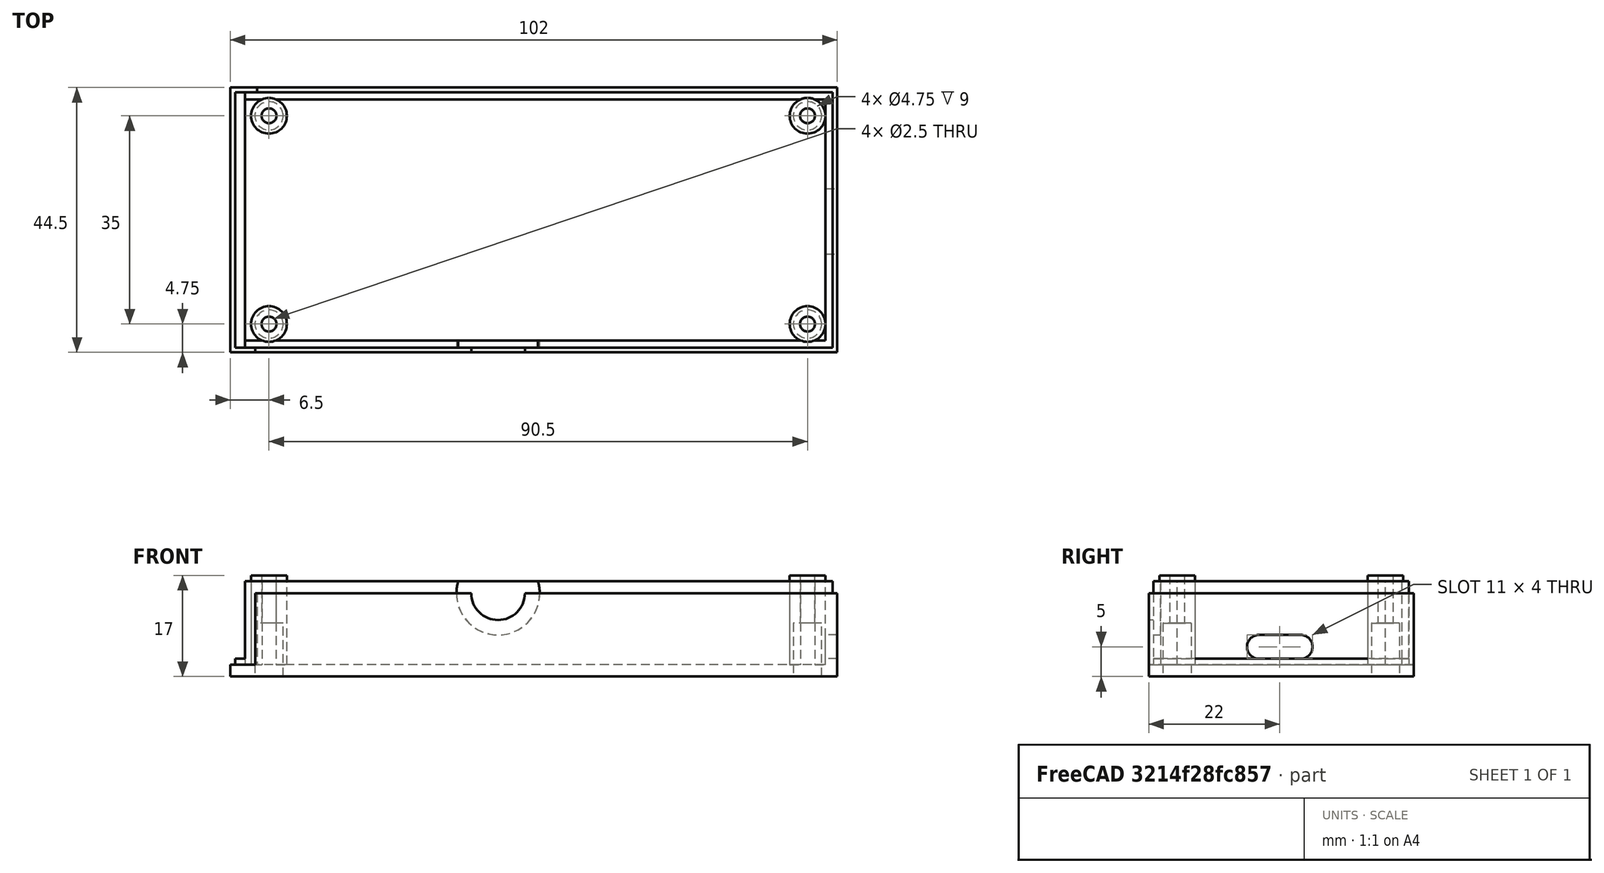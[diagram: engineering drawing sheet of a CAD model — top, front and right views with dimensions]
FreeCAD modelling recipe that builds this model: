
FCSTD DOCUMENT  (FreeCAD 0.20R)
Label: upper_no_battery
License: All rights reserved
LicenseURL: http://en.wikipedia.org/wiki/All_rights_reserved
objects: Sketcher::SketchObject×11, PartDesign::Pocket×9, PartDesign::Pad×2, PartDesign::Plane×1, PartDesign::Body×1
note: 35 computed .brp shape members not serialized (recipe doc carries the construction recipe); baked Part::Feature solids carry a one-line shape summary decoded from their .brp

FEATURE [Sketcher::SketchObject] Sketch  label="sketch_lower_base"
  FullyConstrained = true
  MapMode = 5
  Support = -> [XY_Plane]
  sketch-geometry (4):
    g0: LineSegment StartX=0 StartY=0 StartZ=0 EndX=102 EndY=0 EndZ=0
    g1: LineSegment StartX=102 StartY=0 StartZ=0 EndX=102 EndY=44.5 EndZ=0
    g2: LineSegment StartX=102 StartY=44.5 StartZ=0 EndX=0 EndY=44.5 EndZ=0
    g3: LineSegment StartX=0 StartY=44.5 StartZ=0 EndX=0 EndY=0 EndZ=0
  constraints (11):
    c: Coincident(g0,g1)
    c: Coincident(g1,g2)
    c: Coincident(g2,g3)
    c: Coincident(g3,g0)
    c: Horizontal(g0)
    c: Horizontal(g2)
    c: Vertical(g1)
    c: Vertical(g3)
    c: Coincident(g0,g-1)
    c: Distance(g2) = 102
    c: Distance(g3) = 44.5
FEATURE [PartDesign::Pad] Pad  label="pad_lower_base"
  Direction = (0,0,1)
  Length = 16
  Length2 = 10
  Profile = -> Sketch
  ReferenceAxis = -> Sketch [N_Axis]
  Type = 0
FEATURE [Sketcher::SketchObject] Sketch001  label="sketch_lower_base_hole"
  FullyConstrained = true
  MapMode = 5
  Placement = pos=(0,0,16) rot=(0,0,1;0rad)
  Support = -> [Pad]
  sketch-geometry (4):
    g0: LineSegment StartX=2.5 StartY=42.5 StartZ=0 EndX=100 EndY=42.5 EndZ=0
    g1: LineSegment StartX=100 StartY=42.5 StartZ=0 EndX=100 EndY=2 EndZ=0
    g2: LineSegment StartX=100 StartY=2 StartZ=0 EndX=2.5 EndY=2 EndZ=0
    g3: LineSegment StartX=2.5 StartY=2 StartZ=0 EndX=2.5 EndY=42.5 EndZ=0
  constraints (12):
    c: Coincident(g0,g1)
    c: Coincident(g1,g2)
    c: Coincident(g2,g3)
    c: Coincident(g3,g0)
    c: Horizontal(g0)
    c: Horizontal(g2)
    c: Vertical(g1)
    c: Vertical(g3)
    c: DistanceX(g-2,g2) = 2.5
    c: DistanceY(g-1,g2) = 2
    c: Distance(g0) = 97.5
    c: Distance(g1) = 40.5
FEATURE [PartDesign::Pocket] Pocket  label="pocket_lower_base_hole"
  BaseFeature = -> Pad
  Direction = (0,0,-1)
  Length = 14
  Length2 = 5
  Profile = -> Sketch001
  ReferenceAxis = -> Sketch001 [N_Axis]
  Type = 0
FEATURE [Sketcher::SketchObject] Sketch002  label="sketch_board_stands"
  FullyConstrained = true
  MapMode = 5
  Placement = pos=(0,0,2) rot=(0,0,1;0rad)
  Support = -> [Pocket]
  sketch-geometry (4):
    g0: Circle CenterX=6.5 CenterY=39.75 CenterZ=0 NormalX=0 NormalY=0 NormalZ=1 AngleXU=0 Radius=3
    g1: Circle CenterX=97 CenterY=39.75 CenterZ=0 NormalX=0 NormalY=0 NormalZ=1 AngleXU=0 Radius=3
    g2: Circle CenterX=6.5 CenterY=4.75 CenterZ=0 NormalX=0 NormalY=0 NormalZ=1 AngleXU=0 Radius=3
    g3: Circle CenterX=97 CenterY=4.75 CenterZ=0 NormalX=0 NormalY=0 NormalZ=1 AngleXU=0 Radius=3
  constraints (12):
    c: Equal(g0,g1)
    c: Equal(g1,g3)
    c: Equal(g3,g2)
    c: Distance(g0,g1) = 90.5
    c: Distance(g2,g3) = 90.5
    c: Diameter(g1) = 6
    c: Distance(g1,g3) = 35
    c: Distance(g0,g2) = 35
    c: DistanceX(g-2,g1) = 97
    c: DistanceX(g-2,g3) = 97
    c: DistanceY(g-1,g2) = 4.75
    c: DistanceY(g-1,g3) = 4.75
FEATURE [PartDesign::Pad] Pad001  label="pad_board_stands"
  BaseFeature = -> Pocket
  Direction = (0,0,1)
  Length = 15
  Length2 = 10
  Profile = -> Sketch002
  ReferenceAxis = -> Sketch002 [N_Axis]
  Type = 0
FEATURE [PartDesign::Plane] DatumPlane  label="plane_upper"
  Length = 145.79
  MapMode = 5
  Placement = pos=(0,0,-18) rot=(1,0,0;3.14159rad)
  ResizeMode = 0
  Width = 88.2899
FEATURE [Sketcher::SketchObject] Sketch007  label="sketch_screw_holes"
  FullyConstrained = true
  MapMode = 5
  Placement = pos=(0,0,-18) rot=(1,0,0;3.14159rad)
  Support = -> [DatumPlane]
  sketch-geometry (4):
    g0: Circle CenterX=6.5 CenterY=-4.75 CenterZ=0 NormalX=0 NormalY=0 NormalZ=1 AngleXU=0 Radius=1.25
    g1: Circle CenterX=97 CenterY=-4.75 CenterZ=0 NormalX=0 NormalY=0 NormalZ=1 AngleXU=0 Radius=1.25
    g2: Circle CenterX=6.5 CenterY=-39.75 CenterZ=0 NormalX=0 NormalY=0 NormalZ=1 AngleXU=0 Radius=1.25
    g3: Circle CenterX=97 CenterY=-39.75 CenterZ=0 NormalX=0 NormalY=0 NormalZ=1 AngleXU=0 Radius=1.25
  constraints (12):
    c: Equal(g0,g2)
    c: Equal(g2,g3)
    c: Equal(g3,g1)
    c: Diameter(g0) = 2.5
    c: Distance(g3,g1) = 35
    c: Distance(g0,g2) = 35
    c: Distance(g0,g1) = 90.5
    c: Distance(g2,g3) = 90.5
    c: DistanceY(g-1,g0) = -4.75
    c: DistanceY(g-1,g1) = -4.75
    c: DistanceX(g-2,g1) = 97
    c: DistanceX(g-2,g3) = 97
FEATURE [PartDesign::Pocket] Pocket004  label="pocket_screw_holes"
  BaseFeature = -> Pad001
  Direction = (0,0,1)
  Length = 35
  Length2 = 5
  Profile = -> Sketch007
  ReferenceAxis = -> Sketch007 [N_Axis]
  Type = 0
FEATURE [Sketcher::SketchObject] Sketch008  label="sketch_screwdriver_hole"
  FullyConstrained = true
  MapMode = 5
  Placement = pos=(0,0,-18) rot=(1,0,0;3.14159rad)
  Support = -> [DatumPlane]
  sketch-geometry (4):
    g0: Circle CenterX=6.5 CenterY=-4.75 CenterZ=0 NormalX=0 NormalY=0 NormalZ=1 AngleXU=0 Radius=2.375
    g1: Circle CenterX=97 CenterY=-4.75 CenterZ=0 NormalX=0 NormalY=0 NormalZ=1 AngleXU=0 Radius=2.375
    g2: Circle CenterX=6.5 CenterY=-39.75 CenterZ=0 NormalX=0 NormalY=0 NormalZ=1 AngleXU=0 Radius=2.375
    g3: Circle CenterX=97 CenterY=-39.75 CenterZ=0 NormalX=0 NormalY=0 NormalZ=1 AngleXU=0 Radius=2.375
  constraints (12):
    c: Diameter(g0) = 4.75
    c: Equal(g0,g1)
    c: Equal(g1,g2)
    c: Equal(g2,g3)
    c: DistanceY(g-1,g0) = -4.75
    c: DistanceY(g-1,g1) = -4.75
    c: Distance(g3,g2) = 90.5
    c: Distance(g0,g1) = 90.5
    c: Distance(g1,g3) = 35
    c: Distance(g2,g0) = 35
    c: DistanceX(g-2,g3) = 97
    c: DistanceX(g-2,g1) = 97
FEATURE [PartDesign::Pocket] Pocket005  label="pocket_screwdriver_hole"
  BaseFeature = -> Pocket004
  Direction = (0,0,1)
  Length = 27
  Length2 = 5
  Profile = -> Sketch008
  ReferenceAxis = -> Sketch008 [N_Axis]
  Type = 0
FEATURE [Sketcher::SketchObject] Sketch011  label="sketch_esp_usb_hole"
  FullyConstrained = true
  MapMode = 5
  Placement = pos=(102,0,0) rot=(0.57735,0.57735,0.57735;2.0944rad)
  sketch-geometry (4):
    g0: ArcOfCircle CenterX=18.5 CenterY=5 CenterZ=0 NormalX=0 NormalY=0 NormalZ=1 AngleXU=0 Radius=2 StartAngle=1.5708 EndAngle=4.71239
    g1: ArcOfCircle CenterX=25.5 CenterY=5 CenterZ=0 NormalX=0 NormalY=0 NormalZ=1 AngleXU=0 Radius=2 StartAngle=4.71239 EndAngle=7.85398
    g2: LineSegment StartX=18.5 StartY=3 StartZ=0 EndX=25.5 EndY=3 EndZ=0
    g3: LineSegment StartX=25.5 StartY=7 StartZ=0 EndX=18.5 EndY=7 EndZ=0
  constraints (10):
    c: Tangent(g0,g2) = -1.5708
    c: Tangent(g2,g1) = -1.5708
    c: Tangent(g1,g3) = -1.5708
    c: Tangent(g3,g0) = -1.5708
    c: Equal(g0,g1)
    c: Horizontal(g2)
    c: Radius(g1) = 2
    c: Distance(g0,g1) = 7
    c: DistanceY(g-1,g0) = 3
    c: DistanceX(g-2,g0) = 18.5
FEATURE [PartDesign::Pocket] Pocket008  label="pocket_esp_usb_hole"
  BaseFeature = -> Pocket005
  Direction = (-1,0,0)
  Length = 5
  Length2 = 5
  Profile = -> Sketch011
  ReferenceAxis = -> Sketch011 [N_Axis]
  Type = 0
FEATURE [Sketcher::SketchObject] Sketch012  label="sketch_ptt_hole"
  FullyConstrained = true
  MapMode = 5
  Placement = pos=(0,0,0) rot=(1,0,0;1.5708rad)
  Support = -> [Pocket008]
  sketch-geometry (1):
    g0: Circle CenterX=45 CenterY=14 CenterZ=0 NormalX=0 NormalY=0 NormalZ=1 AngleXU=0 Radius=4.5
  constraints (3):
    c: DistanceY(g-1,g0) = 14
    c: Diameter(g0) = 9
    c: DistanceX(g-2,g0) = 45
FEATURE [PartDesign::Pocket] Pocket009  label="pocket_ptt_hole"
  BaseFeature = -> Pocket008
  Direction = (0,1,-2e-16)
  Length = 10
  Length2 = 5
  Profile = -> Sketch012
  ReferenceAxis = -> Sketch012 [N_Axis]
  Type = 0
FEATURE [Sketcher::SketchObject] Sketch013  label="sketch_ptt_hole_rounding"
  FullyConstrained = true
  MapMode = 5
  Placement = pos=(0,2,0) rot=(0,0.707107,0.707107;3.14159rad)
  Support = -> [Pocket009]
  sketch-geometry (1):
    g0: Circle CenterX=-45 CenterY=14 CenterZ=0 NormalX=0 NormalY=0 NormalZ=1 AngleXU=0 Radius=7
  constraints (3):
    c: DistanceX(g-2,g0) = -45
    c: DistanceY(g-1,g0) = 14
    c: Diameter(g0) = 14
FEATURE [PartDesign::Pocket] Pocket010  label="pocket_ptt_hole_rounding"
  BaseFeature = -> Pocket009
  Direction = (0,-1,2e-16)
  Length = 1.2
  Length2 = 5
  Profile = -> Sketch013
  ReferenceAxis = -> Sketch013 [N_Axis]
  Type = 0
FEATURE [Sketcher::SketchObject] Sketch022  label="sketch_face_removal"
  FullyConstrained = true
  MapMode = 5
  Placement = pos=(0,0,16) rot=(0,0,1;0rad)
  sketch-geometry (4):
    g0: LineSegment StartX=0 StartY=44.5 StartZ=0 EndX=2.5 EndY=44.5 EndZ=0
    g1: LineSegment StartX=2.5 StartY=44.5 StartZ=0 EndX=2.5 EndY=0 EndZ=0
    g2: LineSegment StartX=2.5 StartY=0 StartZ=0 EndX=0 EndY=0 EndZ=0
    g3: LineSegment StartX=0 StartY=0 StartZ=0 EndX=0 EndY=44.5 EndZ=0
  constraints (12):
    c: Coincident(g0,g1)
    c: Coincident(g1,g2)
    c: Coincident(g2,g3)
    c: Coincident(g3,g0)
    c: Horizontal(g0)
    c: Horizontal(g2)
    c: Vertical(g1)
    c: Vertical(g3)
    c: PointOnObject(g0,g-2)
    c: PointOnObject(g1,g-1)
    c: Distance(g0) = 2.5
    c: Distance(g1) = 44.5
FEATURE [PartDesign::Pocket] Pocket018  label="pocket_face_removal"
  BaseFeature = -> Pocket010
  Direction = (0,0,-1)
  Length = 13
  Length2 = 5
  Profile = -> Sketch022
  ReferenceAxis = -> Sketch022 [N_Axis]
  Type = 0
FEATURE [Sketcher::SketchObject] Sketch023  label="sketch_outer_facet_removal"
  FullyConstrained = false
  MapMode = 5
  Placement = pos=(0,0,16) rot=(0,0,1;0rad)
  Support = -> [Pocket018]
  sketch-geometry (8):
    g0: LineSegment StartX=2.49905 StartY=44.5 StartZ=0 EndX=102 EndY=44.5 EndZ=0
    g1: LineSegment StartX=102 StartY=44.5 StartZ=0 EndX=102 EndY=0 EndZ=0
    g2: LineSegment StartX=102 StartY=0 StartZ=0 EndX=2.5 EndY=0 EndZ=0
    g3: LineSegment StartX=2.5 StartY=0 StartZ=0 EndX=2.5 EndY=0.8 EndZ=0
    g4: LineSegment StartX=2.5 StartY=0.8 StartZ=0 EndX=101.2 EndY=0.8 EndZ=0
    g5: LineSegment StartX=101.2 StartY=0.8 StartZ=0 EndX=101.2 EndY=43.7 EndZ=0
    g6: LineSegment StartX=101.2 StartY=43.7 StartZ=0 EndX=2.49905 EndY=43.7 EndZ=0
    g7: LineSegment StartX=2.49905 StartY=43.7 StartZ=0 EndX=2.49905 EndY=44.5 EndZ=0
  constraints (23):
    c: Horizontal(g0)
    c: Coincident(g1,g0)
    c: Vertical(g1)
    c: Coincident(g2,g1)
    c: PointOnObject(g2,g-1)
    c: Horizontal(g2)
    c: Coincident(g3,g2)
    c: Vertical(g3)
    c: Coincident(g4,g3)
    c: Horizontal(g4)
    c: Coincident(g5,g4)
    c: Vertical(g5)
    c: Coincident(g6,g5)
    c: Horizontal(g6)
    c: Coincident(g7,g6)
    c: Coincident(g7,g0)
    c: Vertical(g7)
    c: Distance(g7) = 0.8
    c: Equal(g7,g3)
    c: Distance(g5,g1) = 0.8
    c: DistanceX(g-2,g2) = 2.5
    c: DistanceY(g-1,g0) = 44.5
    c: DistanceX(g-2,g0) = 102
FEATURE [PartDesign::Pocket] Pocket019  label="pocket_outer_facet_removal"
  BaseFeature = -> Pocket018
  Direction = (0,0,-1)
  Length = 2
  Length2 = 5
  Profile = -> Sketch023
  ReferenceAxis = -> Sketch023 [N_Axis]
  Type = 0
FEATURE [Sketcher::SketchObject] Sketch024  label="sketch_outer_front_facet_removal"
  FullyConstrained = false
  MapMode = 5
  Placement = pos=(0,0,16) rot=(0,0,1;0rad)
  Support = -> [Pocket019]
  sketch-geometry (8):
    g0: LineSegment StartX=4.16371 StartY=0 StartZ=0 EndX=4.16371 EndY=0.8 EndZ=0
    g1: LineSegment StartX=4.16371 StartY=0.8 StartZ=0 EndX=0.800622 EndY=0.8 EndZ=0
    g2: LineSegment StartX=0.800622 StartY=0.8 StartZ=0 EndX=0.800622 EndY=43.7 EndZ=0
    g3: LineSegment StartX=0.800622 StartY=43.7 StartZ=0 EndX=4.5 EndY=43.7 EndZ=0
    g4: LineSegment StartX=4.5 StartY=43.7 StartZ=0 EndX=4.5 EndY=44.5 EndZ=0
    g5: LineSegment StartX=4.5 StartY=44.5 StartZ=0 EndX=0 EndY=44.5 EndZ=0
    g6: LineSegment StartX=0 StartY=44.5 StartZ=0 EndX=0 EndY=0 EndZ=0
    g7: LineSegment StartX=0 StartY=0 StartZ=0 EndX=4.16371 EndY=0 EndZ=0
  constraints (21):
    c: Coincident(g4,g5)
    c: Coincident(g4,g3)
    c: Coincident(g6,g5)
    c: Coincident(g2,g3)
    c: Coincident(g1,g2)
    c: Coincident(g1,g0)
    c: Coincident(g0,g7)
    c: Coincident(g7,g6)
    c: Distance(g4) = 0.8
    c: Distance(g0) = 0.8
    c: Parallel(g6,g2)
    c: Parallel(g2,g0)
    c: Parallel(g0,g4)
    c: Parallel(g4,g-2)
    c: Parallel(g5,g3)
    c: Parallel(g3,g1)
    c: Parallel(g1,g7)
    c: Parallel(g7,g-1)
    c: Distance(g5) = 4.5
    c: Coincident(g6,g-1)
    c: Distance(g6) = 44.5
FEATURE [PartDesign::Pocket] Pocket020  label="pocket_outer_front_facet_removal"
  BaseFeature = -> Pocket019
  Direction = (0,0,-1)
  Length = 14
  Length2 = 5
  Profile = -> Sketch024
  ReferenceAxis = -> Sketch024 [N_Axis]
  Type = 0
FEATURE [PartDesign::Body] Body
  Group = -> [Sketch,Pad,Sketch001,Pocket,Sketch002,Pad001,DatumPlane,Sketch007,Pocket004,Sketch008,Pocket005,Sketch011,Pocket008,Sketch012,Pocket009,Sketch013,Pocket010,Sketch022,Pocket018,Sketch023,Pocket019,Sketch024,Pocket020]
  Origin = -> Origin
  Tip = -> Pocket020
